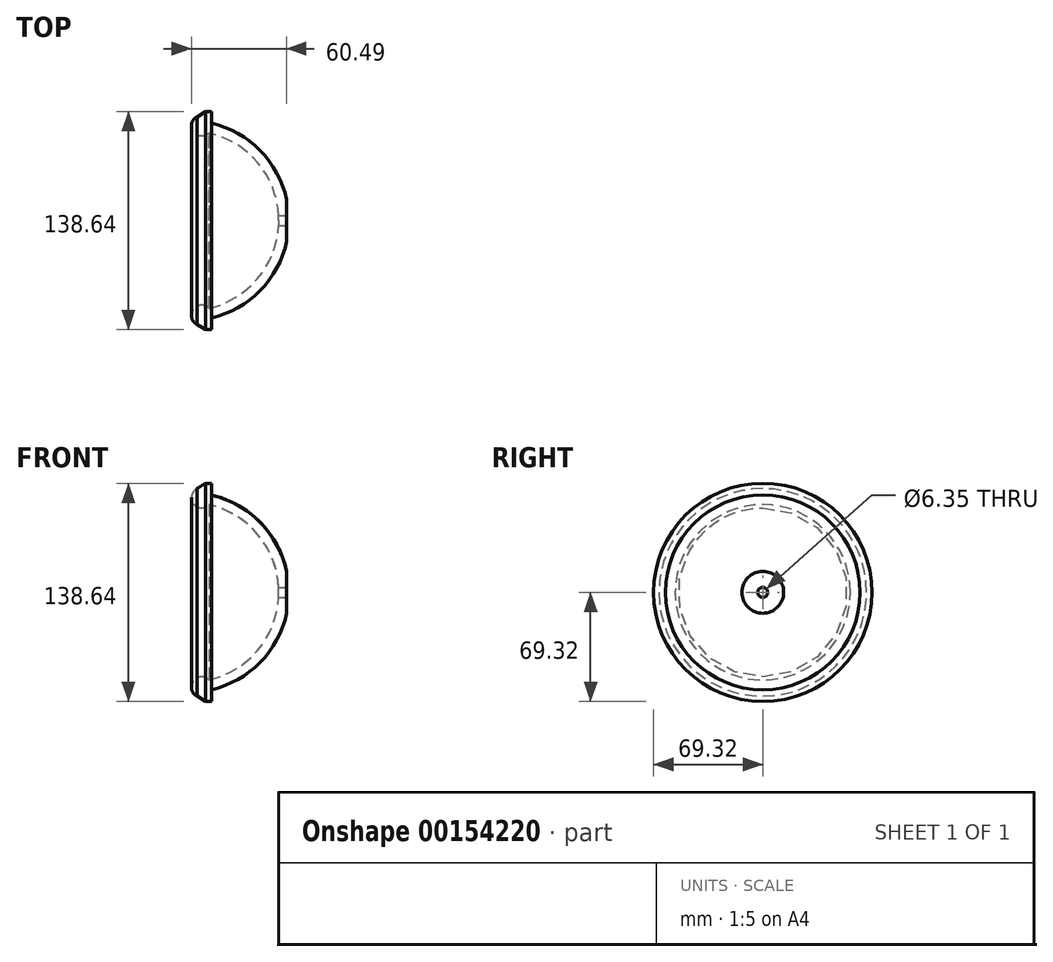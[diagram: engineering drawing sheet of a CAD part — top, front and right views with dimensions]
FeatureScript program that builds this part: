
annotation { "Feature Type Name" : "Feature", "Feature Type Description" : "" }
export const myFeature = defineFeature(function(context is Context, id is Id, definition is map)
    precondition{}
    {
        {
            var Q0;
            Q0=qCreatedBy(makeId("Front.planeOp"),FACE);
            var sketch = newSketch(context, id + "F0", { "sketchPlane" : qUnion([Q0])});
            skCircle(sketch, "E0", {"center": v(0, 0) * mm, "radius": 63.5 * mm});
            skCircle(sketch, "E1", {"center": v(0, 0) * mm, "radius": 57.15 * mm});
            skCircle(sketch, "E2", {"center": v(8.1, 60.15) * mm, "radius": 6.5 * mm});
            skArc(sketch, "E3", {"start": v(27.18, 50.27) * mm, "mid": v(18.8, 53.17) * mm, "end": v(9.96, 53.92) * mm});
            skLineSegment(sketch, "E4", {"start": v(5.08, 65.9) * mm, "end": v(10.67, 69.32) * mm});
            skLineSegment(sketch, "E5", {"start": v(14.38, 61.85) * mm, "end": v(14.38, 69.32) * mm});
            skLineSegment(sketch, "E6", {"start": v(14.38, 69.32) * mm, "end": v(10.67, 69.32) * mm});
            skLineSegment(sketch, "E7", {"start": v(0, 0) * mm, "end": v(63.5, 0) * mm});
            skSolve(sketch);
        }
        {
            var Q0;
            {var subQ3=sQuery(id+"F0.wireOp",EDGE,"E1");var subQ5=makeQuery(id+"F0.imprint","INTERSECT",VERTEX,{"derivedFrom":[subQ3,sQuery(id+"F0.wireOp",EDGE,"E3")]});Q0=makeQuery(id+"F0.imprint","IMPRINT",FACE,{"disambiguationData":[TD([[makeQuery(id+"F0.imprint","IMPRINT",EDGE,{"disambiguationData":[TD([[subQ5,1.0]])],"derivedFrom":subQ3}),-1.0]])]});}
            var Q1;
            {var subQ0=sQuery(id+"F0.wireOp",EDGE,"E2");var subQ4=sQuery(id+"F0.wireOp",EDGE,"E1");var subQ5=makeQuery(id+"F0.imprint","INTERSECT",VERTEX,{"disambiguationData":[OD(0.0)],"derivedFrom":[subQ4,subQ0]});Q1=makeQuery(id+"F0.imprint","IMPRINT",FACE,{"disambiguationData":[TD([[makeQuery(id+"F0.imprint","IMPRINT",EDGE,{"disambiguationData":[TD([[subQ5,-1.0]])],"derivedFrom":subQ4}),-1.0]])]});}
            var Q2;
            {var subQ0=sQuery(id+"F0.wireOp",EDGE,"E2");var subQ1=sQuery(id+"F0.wireOp",EDGE,"E1");var subQ2=makeQuery(id+"F0.imprint","INTERSECT",VERTEX,{"disambiguationData":[OD(0.0)],"derivedFrom":[subQ1,subQ0]});Q2=makeQuery(id+"F0.imprint","IMPRINT",FACE,{"disambiguationData":[TD([[makeQuery(id+"F0.imprint","IMPRINT",EDGE,{"disambiguationData":[TD([[subQ2,-1.0]])],"derivedFrom":subQ1}),1.0]])]});}
            var Q3;
            {var subQ0=sQuery(id+"F0.wireOp",EDGE,"E4");Q3=makeQuery(id+"F0.imprint","IMPRINT",FACE,{"disambiguationData":[TD([[makeQuery(id+"F0.imprint","IMPRINT",EDGE,{"derivedFrom":subQ0}),-1.0]])]});}
            var Q4;
            {var subQ0=sQuery(id+"F0.wireOp",EDGE,"E2");var subQ4=makeQuery(id+"F0.imprint","INTERSECT",VERTEX,{"derivedFrom":[subQ0,sQuery(id+"F0.wireOp",EDGE,"E4")]});Q4=makeQuery(id+"F0.imprint","IMPRINT",FACE,{"disambiguationData":[TD([[makeQuery(id+"F0.imprint","IMPRINT",EDGE,{"disambiguationData":[TD([[subQ4,-1.0]])],"derivedFrom":subQ0}),1.0]])]});}
            var Q5;
            Q5=sQuery(id+"F0.wireOp",EDGE,"E7");
            revolve(context, id + "F1", {"entities" : qUnion([Q0, Q1, Q2, Q3, Q4]), "axis" : qUnion([Q5]), "revolveType" : RevolveType.FULL});
        }
        {
            var Q0;
            Q0=qCreatedBy(makeId("Right.planeOp"),FACE);
            cPlane(context, id + "F2", {"entities" : qUnion([Q0]), "cplaneType" : CPlaneType.OFFSET, "offset" : 71.12 * mm, "width" : 152.4 * mm, "height" : 152.4 * mm});
        }
        {
            var Q0;
            Q0=qCreatedBy(id+"F2.planeOp",FACE);
            var sketch = newSketch(context, id + "F3", { "sketchPlane" : qUnion([Q0])});
            skPoint(sketch, "E8.middle", {"position": v(0, 0) * mm});
            skPoint(sketch, "E8.left.end.orphan", {"position": v(35.88, 35.88) * mm});
            skPoint(sketch, "E8.bottom.start.orphan", {"position": v(35.88, -35.88) * mm});
            skPoint(sketch, "E8.right.end.orphan", {"position": v(-35.88, 35.88) * mm});
            skPoint(sketch, "E8.right.start.orphan", {"position": v(-35.88, -35.88) * mm});
            skCircle(sketch, "E9", {"center": v(0, 0) * mm, "radius": 13.46 * mm});
            skCircle(sketch, "E10", {"center": v(0, 0) * mm, "radius": 3.18 * mm});
            skSolve(sketch);
        }
        {
            var Q0;
            Q0=makeQuery(id+"F3.imprint","IMPRINT",FACE,{"disambiguationData":[TD([[makeQuery(id+"F3.imprint","IMPRINT",EDGE,{"derivedFrom":sQuery(id+"F3.wireOp",EDGE,"E10")}),1.0]])]});
            extrude(context, id + "F4", {"entities" : qUnion([Q0]), "operationType" : NewBodyOperationType.REMOVE, "oppositeDirection" : true, "depth" : 25.4 * mm});
        }
        {
            var Q0;
            Q0=makeQuery(id+"F3.imprint","IMPRINT",FACE,{"disambiguationData":[TD([[makeQuery(id+"F3.imprint","IMPRINT",EDGE,{"derivedFrom":sQuery(id+"F3.wireOp",EDGE,"E9")}),1.0]])]});
            extrude(context, id + "F5", {"entities" : qUnion([Q0]), "operationType" : NewBodyOperationType.REMOVE, "oppositeDirection" : true, "depth" : 9.02 * mm});
        }
    });
